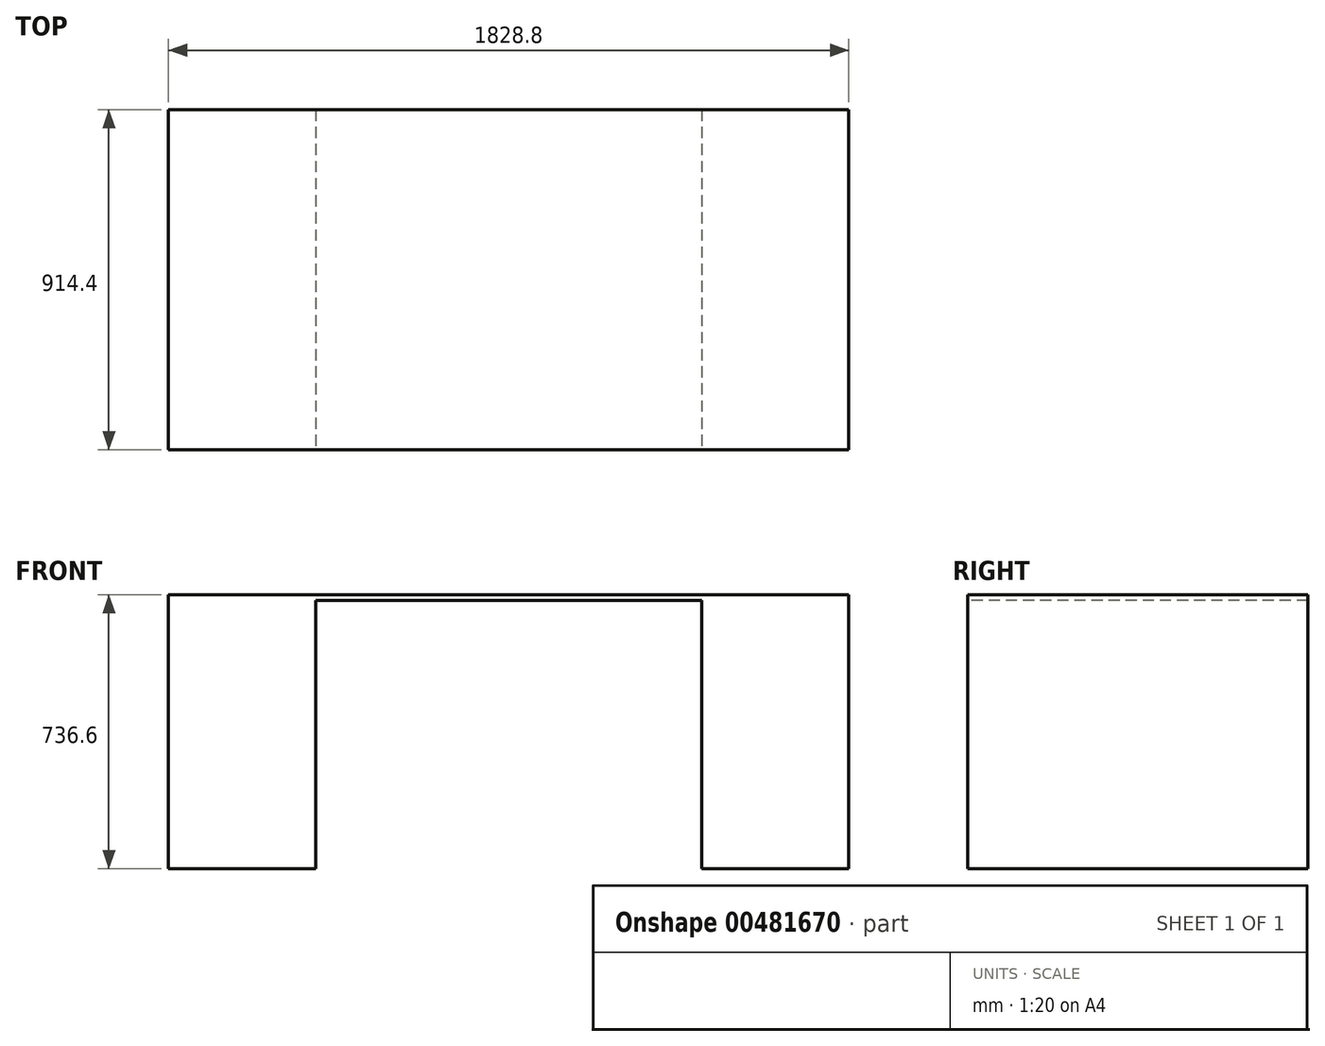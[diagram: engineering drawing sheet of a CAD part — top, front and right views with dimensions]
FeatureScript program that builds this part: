
annotation { "Feature Type Name" : "Feature", "Feature Type Description" : "" }
export const myFeature = defineFeature(function(context is Context, id is Id, definition is map)
    precondition{}
    {
        {
            var Q0;
            Q0=qCreatedBy(makeId("Top.planeOp"),FACE);
            var sketch = newSketch(context, id + "F0", { "sketchPlane" : qUnion([Q0])});
            skLineSegment(sketch, "E0.bottom", {"start": v(0, 0) * mm, "end": v(1828.8, 0) * mm});
            skLineSegment(sketch, "E0.top", {"start": v(0, 914.4) * mm, "end": v(1828.8, 914.4) * mm});
            skLineSegment(sketch, "E0.left", {"start": v(0, 0) * mm, "end": v(0, 914.4) * mm});
            skLineSegment(sketch, "E0.right", {"start": v(1828.8, 0) * mm, "end": v(1828.8, 914.4) * mm});
            skSolve(sketch);
        }
        {
            var Q0;
            Q0=makeQuery(id+"F0.imprint","IMPRINT",FACE,{"disambiguationData":[TD([[makeQuery(id+"F0.imprint","IMPRINT",EDGE,{"derivedFrom":sQuery(id+"F0.wireOp",EDGE,"E0.bottom")}),1.0]])]});
            extrude(context, id + "F1", {"entities" : qUnion([Q0]), "depth" : -736.6 * mm});
        }
        {
            var Q0;
            Q0=makeQuery(id+"F1.opExtrude","SWEPT_FACE",FACE,{"disambiguationData":[OSD([sQuery(id+"F0.wireOp",EDGE,"E0.bottom")])]});
            var sketch = newSketch(context, id + "F2", { "sketchPlane" : qUnion([Q0])});
            skLineSegment(sketch, "E1.bottom", {"start": v(395.84, -14.74) * mm, "end": v(1432.96, -14.74) * mm});
            skLineSegment(sketch, "E1.top", {"start": v(395.84, -736.6) * mm, "end": v(1432.96, -736.6) * mm});
            skLineSegment(sketch, "E1.left", {"start": v(395.84, -14.74) * mm, "end": v(395.84, -736.6) * mm});
            skLineSegment(sketch, "E1.right", {"start": v(1432.96, -14.74) * mm, "end": v(1432.96, -736.6) * mm});
            skLineSegment(sketch, "E2", {"start": v(395.84, -14.74) * mm, "end": v(0, -14.74) * mm, "construction": true});
            skLineSegment(sketch, "E3", {"start": v(1432.96, -14.74) * mm, "end": v(1828.8, -14.74) * mm, "construction": true});
            skSolve(sketch);
        }
        {
            var Q0;
            Q0=makeQuery(id+"F2.imprint","IMPRINT",FACE,{"disambiguationData":[TD([[makeQuery(id+"F2.imprint","IMPRINT",EDGE,{"derivedFrom":sQuery(id+"F2.wireOp",EDGE,"E1.bottom")}),-1.0]])]});
            extrude(context, id + "F3", {"entities" : qUnion([Q0]), "operationType" : NewBodyOperationType.REMOVE, "endBound" : BoundingType.THROUGH_ALL, "oppositeDirection" : true, "depth" : 25.4 * mm});
        }
    });
